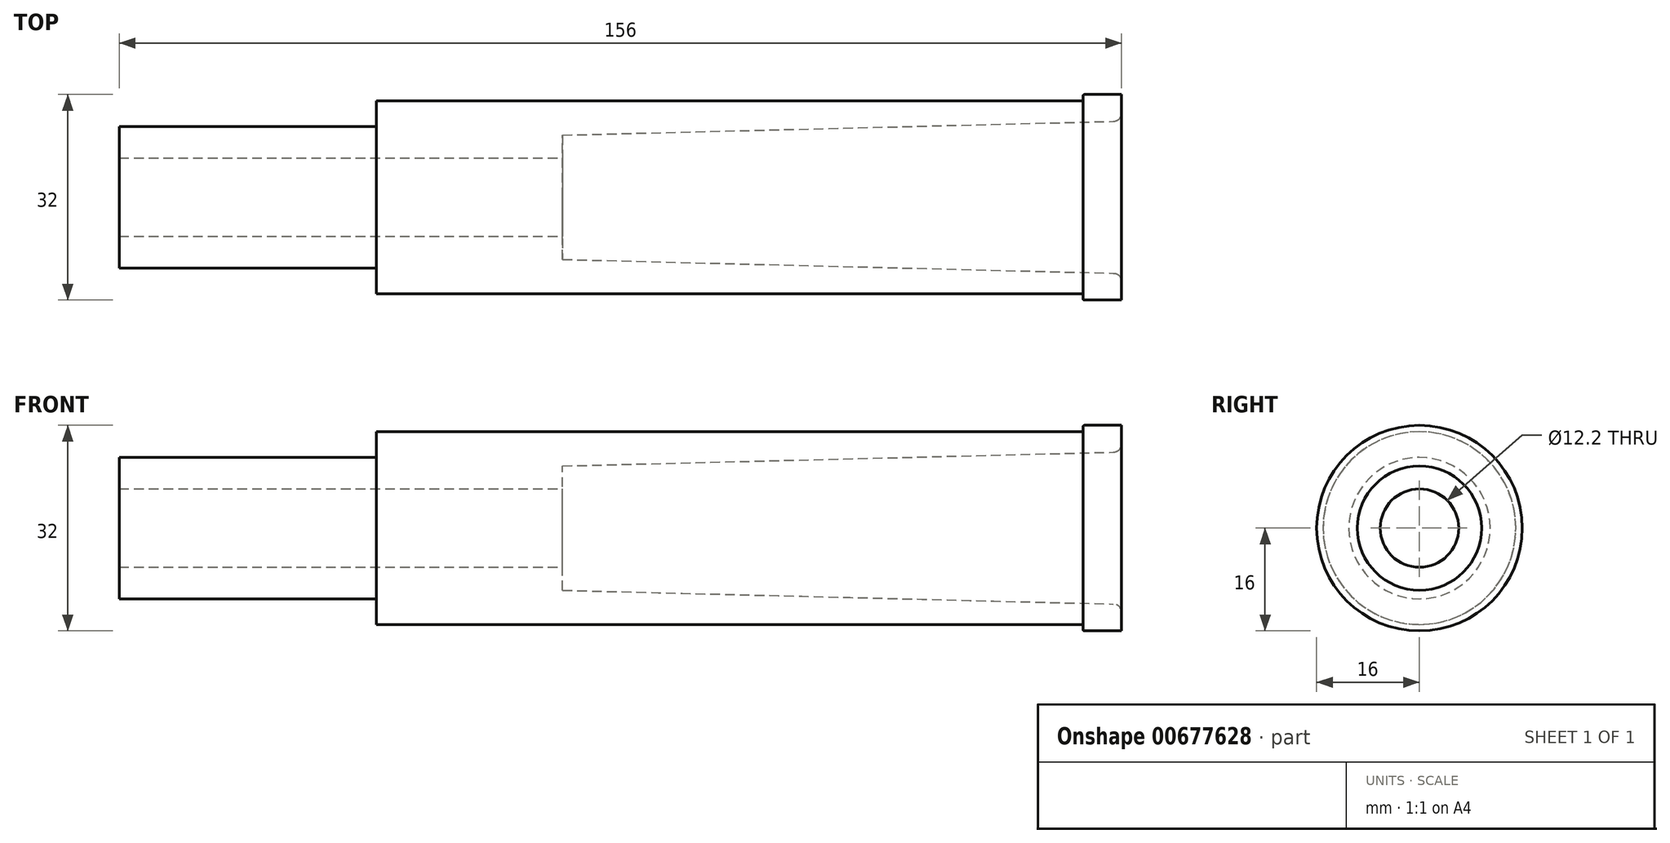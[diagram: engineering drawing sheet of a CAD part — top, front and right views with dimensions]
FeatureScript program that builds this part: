
annotation { "Feature Type Name" : "Feature", "Feature Type Description" : "" }
export const myFeature = defineFeature(function(context is Context, id is Id, definition is map)
    precondition{}
    {
        {
            var Q0;
            Q0=qCreatedBy(makeId("Top.planeOp"),FACE);
            var sketch = newSketch(context, id + "F0", { "sketchPlane" : qUnion([Q0])});
            skLineSegment(sketch, "E0.bottom", {"start": v(47, 16) * mm, "end": v(53, 16) * mm});
            skLineSegment(sketch, "E0.top", {"start": v(47, -16) * mm, "end": v(53, -16) * mm});
            skLineSegment(sketch, "E0.left", {"start": v(-63, 15) * mm, "end": v(-63, 11) * mm});
            skLineSegment(sketch, "E0.right", {"start": v(53, 16) * mm, "end": v(53, -16) * mm});
            skLineSegment(sketch, "E1.bottom", {"start": v(-103, 11) * mm, "end": v(-63, 11) * mm});
            skLineSegment(sketch, "E1.top", {"start": v(-103, -11) * mm, "end": v(-63, -11) * mm});
            skLineSegment(sketch, "E1.left", {"start": v(-103, 11) * mm, "end": v(-103, -11) * mm});
            skLineSegment(sketch, "E2.bottom", {"start": v(-63, -15) * mm, "end": v(47, -15) * mm});
            skLineSegment(sketch, "E2.top", {"start": v(-63, 15) * mm, "end": v(47, 15) * mm});
            skLineSegment(sketch, "E2.right", {"start": v(47, -16) * mm, "end": v(47, -15) * mm});
            skLineSegment(sketch, "E3", {"start": v(0, 0) * mm, "end": v(-103, 0) * mm});
            skLineSegment(sketch, "E4", {"start": v(53, 0) * mm, "end": v(0, 0) * mm});
            skLineSegment(sketch, "E5", {"start": v(0, 0) * mm, "end": v(47, 0) * mm});
            skLineSegment(sketch, "E6.trimOffspring", {"start": v(47, 15) * mm, "end": v(47, 16) * mm});
            skLineSegment(sketch, "E7.trimOffspring", {"start": v(-63, 11) * mm, "end": v(-63, 14) * mm});
            skPoint(sketch, "E8.endSnap0", {"position": v(-63, -13.5) * mm});
            skPoint(sketch, "E9.trimOffspring.start.orphan", {"position": v(-63, -16) * mm});
            skLineSegment(sketch, "E10", {"start": v(-63, -11) * mm, "end": v(-63, -15) * mm});
            skSolve(sketch);
        }
        {
            var Q0;
            {var subQ6=sQuery(id+"F0.wireOp",EDGE,"E0.top");Q0=makeQuery(id+"F0.imprint","IMPRINT",FACE,{"disambiguationData":[TD([[makeQuery(id+"F0.imprint","IMPRINT",EDGE,{"derivedFrom":subQ6}),1.0]])]});}
            var Q1;
            {var subQ6=sQuery(id+"F0.wireOp",EDGE,"E1.top");Q1=makeQuery(id+"F0.imprint","IMPRINT",FACE,{"disambiguationData":[TD([[makeQuery(id+"F0.imprint","IMPRINT",EDGE,{"derivedFrom":subQ6}),1.0]])]});}
            var Q2;
            Q2=sQuery(id+"F0.wireOp",EDGE,"E3");
            revolve(context, id + "F1", {"entities" : qUnion([Q0, Q1]), "axis" : qUnion([Q2]), "revolveType" : RevolveType.FULL});
        }
        {
            var Q0;
            Q0=qCreatedBy(makeId("Front.planeOp"),FACE);
            var sketch = newSketch(context, id + "F2", { "sketchPlane" : qUnion([Q0])});
            skLineSegment(sketch, "E11", {"start": v(-34, 9.68) * mm, "end": v(-34, -9.68) * mm});
            skLineSegment(sketch, "E12", {"start": v(-34, 9.68) * mm, "end": v(53, 11.85) * mm});
            skLineSegment(sketch, "E13", {"start": v(53, 11.85) * mm, "end": v(53, -11.85) * mm});
            skLineSegment(sketch, "E14", {"start": v(53, -11.85) * mm, "end": v(-34, -9.68) * mm});
            skLineSegment(sketch, "E15", {"start": v(0, 0) * mm, "end": v(-34, 0) * mm});
            skLineSegment(sketch, "E16", {"start": v(53, 0) * mm, "end": v(0, 0) * mm});
            skLineSegment(sketch, "E17.bottom", {"start": v(-134, 6.1) * mm, "end": v(-34, 6.1) * mm});
            skLineSegment(sketch, "E17.top", {"start": v(-134, -6.1) * mm, "end": v(-34, -6.1) * mm});
            skLineSegment(sketch, "E17.left", {"start": v(-134, 6.1) * mm, "end": v(-134, -6.1) * mm});
            skLineSegment(sketch, "E17.right", {"start": v(-34, 6.1) * mm, "end": v(-34, -6.1) * mm});
            skLineSegment(sketch, "E18", {"start": v(-134, 0) * mm, "end": v(-34, 0) * mm});
            skSolve(sketch);
        }
        {
            var Q0;
            {var subQ2=sQuery(id+"F2.wireOp",EDGE,"E12");Q0=makeQuery(id+"F2.imprint","IMPRINT",FACE,{"disambiguationData":[TD([[makeQuery(id+"F2.imprint","IMPRINT",EDGE,{"derivedFrom":subQ2}),-1.0]])]});}
            var Q1;
            {var subQ0=sQuery(id+"F2.wireOp",EDGE,"E17.bottom");Q1=makeQuery(id+"F2.imprint","IMPRINT",FACE,{"disambiguationData":[TD([[makeQuery(id+"F2.imprint","IMPRINT",EDGE,{"derivedFrom":subQ0}),-1.0]])]});}
            var Q2;
            Q2=sQuery(id+"F0.wireOp",EDGE,"E4");
            revolve(context, id + "F3", {"operationType" : NewBodyOperationType.REMOVE, "entities" : qUnion([Q0, Q1]), "axis" : qUnion([Q2]), "revolveType" : RevolveType.FULL});
        }
        {
            var Q0;
            Q0=makeQuery(id+"F3.boolean.opBoolean","INTERSECT",EDGE,{"derivedFrom":[makeQuery(id+"F1.opRevolve","SWEPT_FACE",FACE,{"disambiguationData":[OSD([sQuery(id+"F0.wireOp",EDGE,"E0.right")])]}),makeQuery(id+"F3.opRevolve","SWEPT_FACE",FACE,{"disambiguationData":[OSD([sQuery(id+"F2.wireOp",EDGE,"E12")])]})]});
            fillet(context, id + "F4", {"entities" : qUnion([Q0]), "radius" : 1.3 * mm, "tangentPropagation" : true, "allowEdgeOverflow" : false});
        }
        {
            var Q0;
            Q0=makeQuery(id+"F1.opRevolve","SWEPT_EDGE",EDGE,{"disambiguationData":[OSD([sQuery(id+"F0.wireOp",EDGE,"E0.top"),sQuery(id+"F0.wireOp",EDGE,"E2.right")])]});
            var Q1;
            Q1=makeQuery(id+"F1.opRevolve","SWEPT_EDGE",EDGE,{"disambiguationData":[OSD([sQuery(id+"F0.wireOp",EDGE,"E2.bottom"),sQuery(id+"F0.wireOp",EDGE,"E2.right")])]});
            fillet(context, id + "F5", {"entities" : qUnion([Q0, Q1]), "radius" : .2 * mm, "tangentPropagation" : true, "allowEdgeOverflow" : false});
        }
    });
